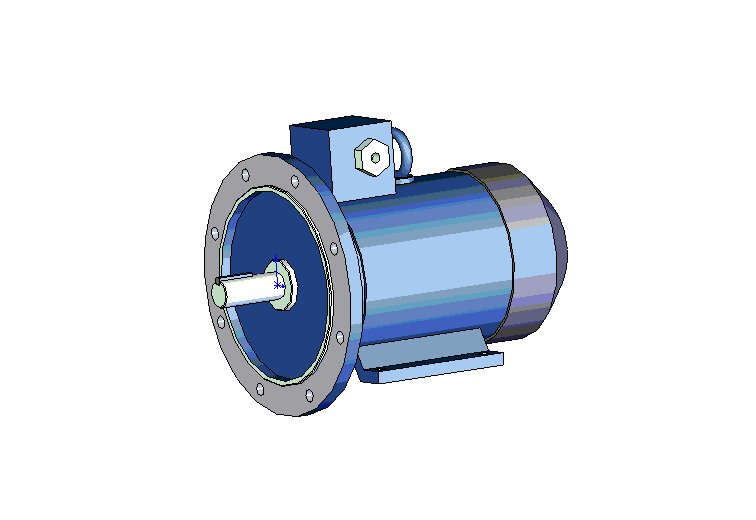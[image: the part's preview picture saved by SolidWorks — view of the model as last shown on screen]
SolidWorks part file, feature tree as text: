
SOLIDWORKS PART (.sldprt)
format: sldprt  version: not decoded by parser v0  size: 653,824 bytes
history: native  units: mm
features: sketch x18, extrude x12, plane x4, cut_extrude x4, chamfer x3, material x1, sweep x1 (+10 scaffold rows collapsed)
feature tree (53):
  scaffold x10  (default folders/planes/origin — collapsed)
  material  "Ст.3 ГОСТ 380-88"
  plane  "Спереди"
  plane  "Сверху"
  plane  "Справа"
  sketch  "Эскиз1"  dims[D1=32.0mm]
  extrude  "Вытянуть1"  Depth=80mm
  sketch  "Эскиз2"  dims[D1=300.0mm]
  extrude  "Вытянуть2"  Depth=17mm
  sketch  "Эскиз3"  dims[D1=8.0mm D2=8.0mm D3=35.0mm]
  extrude  "Вытянуть3"  Depth=45mm
  sketch  "Эскиз4"  dims[D1=230.0mm D2=218.0mm]
  extrude  "Вытянуть4"  Depth=4mm
  sketch  "Эскиз5"  dims[D1=218.0mm D2=120.0mm]
  cut_extrude  "Вырез-Вытянуть1"  Depth=8mm
  chamfer  "Фаска1"  Distance=1mm Angle=45deg
  sketch  "Эскиз6"  dims[c1.D2=15.0mm c1.D1=~77.878668mm c2.D1=22.5deg c2.D3=132.5mm c2.D4=132.5mm c2.D5=132.5mm]
  cut_extrude  "Вырез-Вытянуть2"  [1 undecoded]
  sketch  "Эскиз7"  dims[D1=190.0mm]
  extrude  "Вытянуть5"  Depth=39mm
  sketch  "Эскиз8"  dims[D1=196.0mm]
  extrude  "Вытянуть6"  Depth=199mm
  sketch  "Эскиз9"  dims[D1=202.0mm]
  extrude  "Вытянуть7"  Depth=100mm
  chamfer  "Фаска2"  Distance=42mm Angle=45deg
  sketch  "Эскиз10"  dims[c1.D1=14.0mm c1.D2=14.0mm c1.D3=~80.531247mm c2.D3=30.0deg c2.D4=110.0mm c2.D5=80.0mm c2.D6=112.0mm c2.D7=92.0mm]
  extrude  "Вытянуть8"  Depth=170mm
  sketch  "Эскиз11"  dims[c1.D2=12.0mm c1.D5=12.0mm c1.D1=150.0mm c1.D3=95.0mm c1.D4=90.0deg c2.D5=140.0mm c2.D6=190.0mm c2.D7=190.0mm c2.D8=70.0mm c2.D9=210.0mm]
  cut_extrude  "Вырез-Вытянуть3"  [1 undecoded]
  sketch  "Эскиз12"  dims[D1=85.0mm D2=80.0mm D3=1.0mm]
  extrude  "Вытянуть9"  Depth=173mm
  sketch  "Эскиз13"  dims[D1=40.0mm D2=170.0mm]
  extrude  "Вытянуть10"  Depth=103mm
  chamfer  "Фаска3"  Distance=1mm Angle=45deg
  plane  "Плоскость1"  Offset=170mm
  sketch  "Эскиз14"  dims[D1=50.0mm]
  sketch  "Эскиз15"  dims[D1=12.0mm D2=50.0mm]
  sweep  "По траектории1"
  sketch  "Эскиз16"  dims[D1=20.0mm D2=35.0mm D3=42.5mm]
  extrude  "Вытянуть11"  Depth=14mm
  sketch  "Эскиз17"  dims[D1=~42.85476mm]
  extrude  "Вытянуть12"  Depth=14mm
  sketch  "Эскиз18"  dims[D1=12.0mm]
  cut_extrude  "Вырез-Вытянуть4"  Depth=14mm
decode coverage: 35 of 38 modeling features carry decoded parameters
note: ~ marks probable driven/reference dimensions
note: 2 parameter values undecoded
note: suppression state not decoded; provenance and decode notes live in map.json
